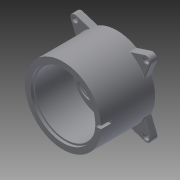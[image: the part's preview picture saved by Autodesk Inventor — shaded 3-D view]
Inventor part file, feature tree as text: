
AUTODESK INVENTOR PART (.ipt)
format: ipt  version: 2013 (Build 170138000, 138)  size: 620,032 bytes
history: native  units: in
note: dims shown in document units (in); Inventor stores cm internally (conversion verified against a paired STEP export)
features: extrude x17, sketch x17, reference x4, fillet x1
ambient origin geometry x8: Origin, YZ Plane, XZ Plane, XY Plane, X Axis, Y Axis, Z Axis, Center Point
bodies: Solid1 (feature_tree)
feature tree (39):
  extrude  "Extrusion1"  Depth=0.1969in TaperAngle=0.0deg
  extrude  "Extrusion14"  Depth=1.3953in TaperAngle=0.0deg
  extrude  "Extrusion15"  Depth=0.6339in
  extrude  "Extrusion39"  Depth=0.0394in
  extrude  "Extrusion17"  Depth=0.315in TaperAngle=0.0deg
  extrude  "Extrusion18"  Depth=0.2756in TaperAngle=0.0deg
  extrude  "Extrusion19"  Depth=0.2362in TaperAngle=0.0deg
  extrude  "Extrusion20"  Depth=0.1969in TaperAngle=0.0deg
  extrude  "Extrusion21"  Depth=0.1575in TaperAngle=0.0deg
  extrude  "Extrusion22"  Depth=0.1181in TaperAngle=0.0deg
  extrude  "Extrusion23"  Depth=0.0787in TaperAngle=0.0deg
  extrude  "Extrusion24"  Depth=0.0394in TaperAngle=0.0deg
  extrude  "Extrusion25"  Depth=0.9843in
  extrude  "Extrusion38"  Depth=0.1102in
  sketch  "Sketch40"  dims[d137=0.0394in d138=0.0394in d139=0.0in]
  extrude  "Extrusion40"  Depth=2.3622in
  extrude  "Extrusion41"  Depth=1.1002in
  extrude  "Extrusion42"  Depth=2.2in
  fillet  "Fillet1"  Radius=0.1575in
  sketch  "Sketch1"  dims[d9=0.1969in d10=0.0in]
  reference  "Reference2"
  reference  "Reference3"
  reference  "Reference4"
  reference  "Reference5"
  sketch  "Sketch15"  dims[d11=0.1181in d12=0.1181in d35=0.3937in d36=0.5906in d37=0.7874in d38=0.9843in d39=0.3937in d40=0.5906in d41=1.1811in d42=1.378in d43=1.5748in d44=1.7717in d94=0.1969in d95=0.0in]
  sketch  "Sketch17"  dims[d96=1.811in d100=1.3953in d101=0.0in]
  sketch  "Sketch18"  dims[d111=0.8189in d112=0.6339in]
  sketch  "Sketch19"  dims[d113=0.4331in d114=0.0in d115=0.0394in]
  sketch  "Sketch20"  dims[d116=0.0394in d117=0.315in d118=0.0in]
  sketch  "Sketch21"  dims[d119=0.0394in d120=0.2756in d121=0.0in]
  sketch  "Sketch22"  dims[d122=0.0394in d123=0.2362in d124=0.0in]
  sketch  "Sketch23"  dims[d125=0.0394in d126=0.1969in d127=0.0in]
  sketch  "Sketch24"  dims[d128=0.0394in d129=0.1575in d130=0.0in]
  sketch  "Sketch25"  dims[d131=0.0394in d132=0.1181in d133=0.0in]
  sketch  "Sketch39"  dims[d134=0.0394in d135=0.0787in d136=0.0in]
  sketch  "Sketch41"  dims[d217=0.9843in d219=0.9843in]
  sketch  "Sketch42"  dims[d220=0.063in d221=0.0in d222=0.1102in]
  sketch  "Sketch43"  dims[d223=0.2756in d231=2.3622in]
  sketch  "Sketch44"  dims[d233=1.5748in d234=1.1002in d264=2.2in d287=0.1575in d288=0.0787in d289=0.0in d291=2.1in d292=1.95in d293=0.1102in d294=0.1102in d295=1.0651in d296=1.0651in d297=2.2441in d298=1.2179in d299=1.122in d300=1.0651in d301=0.1378in d302=1.0651in d303=1.122in d304=0.1575in d305=0.1575in d306=1.811in d307=2.2441in d308=1.811in d310=1.9055in d311=0.0787in d312=0.0in d313=0.2992in d314=0.0in d315=0.1181in d317=1.0236in d318=0.1181in d319=0.0866in d320=0.1575in d321=0.0512in d323=0.1181in d324=0.0in d325=0.0197in]
